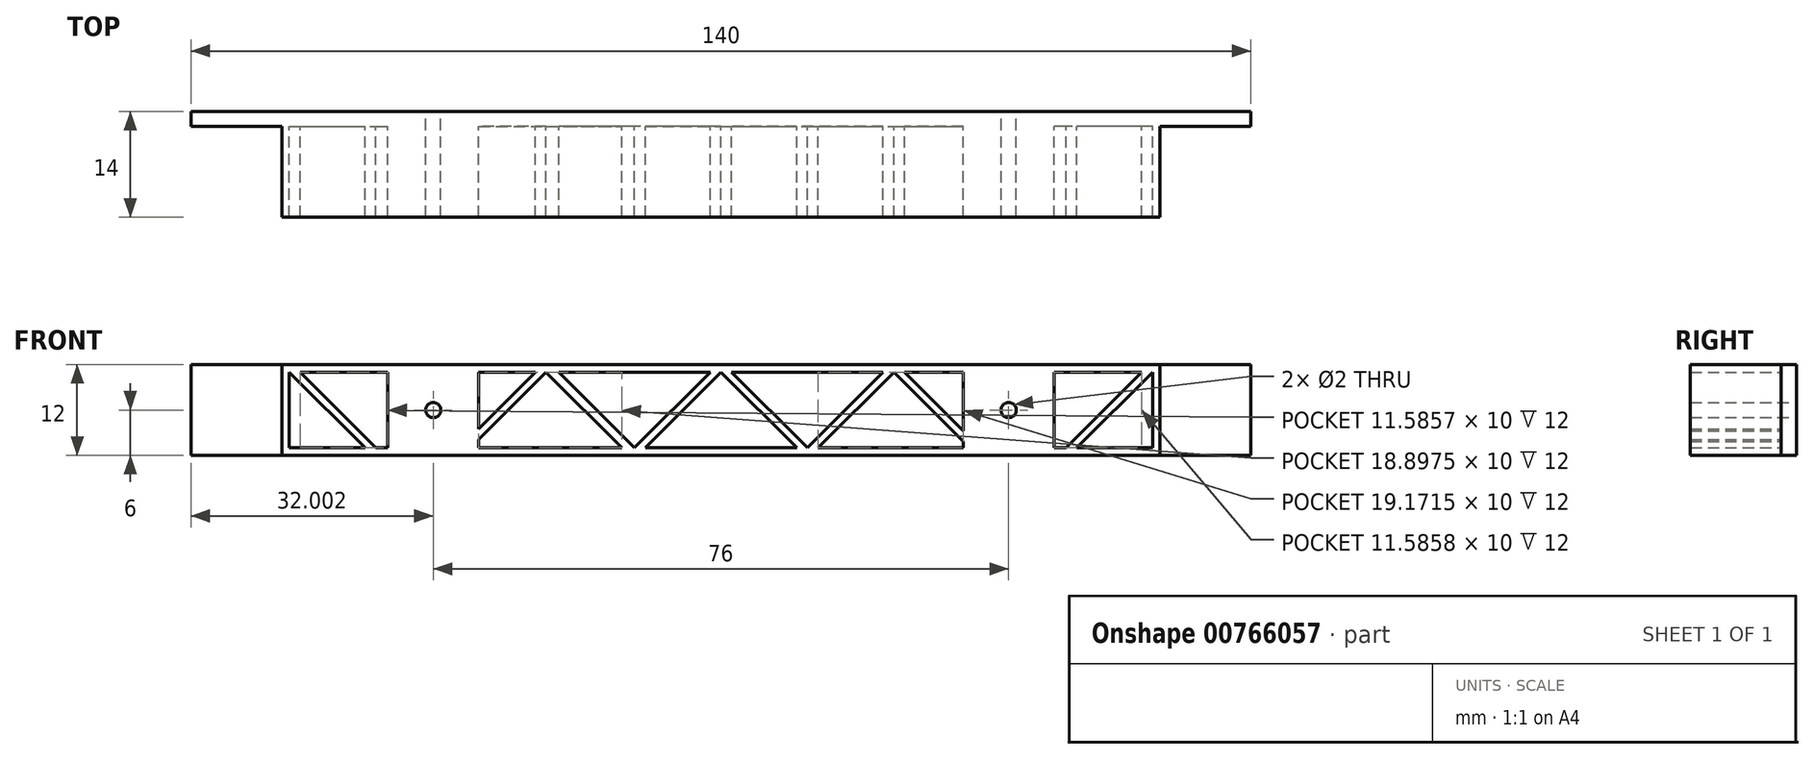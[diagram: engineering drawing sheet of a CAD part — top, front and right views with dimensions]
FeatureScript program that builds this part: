
annotation { "Feature Type Name" : "Feature", "Feature Type Description" : "" }
export const myFeature = defineFeature(function(context is Context, id is Id, definition is map)
    precondition{}
    {
        {
            var Q0;
            Q0=qCreatedBy(makeId("Front.planeOp"),FACE);
            var sketch = newSketch(context, id + "F0", { "sketchPlane" : qUnion([Q0])});
            skLineSegment(sketch, "E0.bottom", {"start": v(-41.02, 0) * mm, "end": v(98.98, 0) * mm});
            skLineSegment(sketch, "E0.top", {"start": v(-41.02, -12) * mm, "end": v(98.98, -12) * mm});
            skLineSegment(sketch, "E0.left", {"start": v(-41.02, 0) * mm, "end": v(-41.02, -12) * mm});
            skLineSegment(sketch, "E0.right", {"start": v(98.98, 0) * mm, "end": v(98.98, -12) * mm});
            skCircle(sketch, "E1", {"center": v(-9.02, -6) * mm, "radius": 1 * mm});
            skCircle(sketch, "E2", {"center": v(66.98, -6) * mm, "radius": 1 * mm});
            skSolve(sketch);
        }
        {
            var Q0;
            Q0=makeQuery(id+"F0.imprint","IMPRINT",FACE,{"disambiguationData":[TD([[makeQuery(id+"F0.imprint","IMPRINT",EDGE,{"derivedFrom":sQuery(id+"F0.wireOp",EDGE,"E0.bottom")}),-1.0]])]});
            extrude(context, id + "F1", {"entities" : qUnion([Q0]), "depth" : 2 * mm, "offsetDistance" : 25 * mm});
        }
        {
            var Q0;
            Q0=makeQuery(id+"F1.opExtrude","CAP_FACE",FACE,{"disambiguationData":[OSD([sQuery(id+"F0.wireOp",EDGE,"E0.bottom"),sQuery(id+"F0.wireOp",EDGE,"E0.top"),sQuery(id+"F0.wireOp",EDGE,"E0.left"),sQuery(id+"F0.wireOp",EDGE,"E0.right"),sQuery(id+"F0.wireOp",EDGE,"E1"),sQuery(id+"F0.wireOp",EDGE,"E2")])],"isStart":false});
            var sketch = newSketch(context, id + "F2", { "sketchPlane" : qUnion([Q0])});
            skLineSegment(sketch, "E3", {"start": v(-29.02, 0) * mm, "end": v(-29.02, -12) * mm});
            skLineSegment(sketch, "E4", {"start": v(86.98, 0) * mm, "end": v(86.98, -12) * mm});
            skLineSegment(sketch, "E5", {"start": v(-15.02, 0) * mm, "end": v(-15.02, -12) * mm});
            skLineSegment(sketch, "E6", {"start": v(-3.02, 0) * mm, "end": v(-3.02, -12) * mm});
            skLineSegment(sketch, "E7", {"start": v(-28.02, -1) * mm, "end": v(-28.02, -11) * mm});
            skLineSegment(sketch, "E8", {"start": v(-28.02, -11) * mm, "end": v(-15.02, -11) * mm});
            skLineSegment(sketch, "E9", {"start": v(-28.02, -1) * mm, "end": v(-15.02, -1) * mm});
            skLineSegment(sketch, "E10", {"start": v(60.98, 0) * mm, "end": v(60.98, -12) * mm});
            skLineSegment(sketch, "E11", {"start": v(72.98, 0) * mm, "end": v(72.98, -12) * mm});
            skLineSegment(sketch, "E12", {"start": v(85.98, -1) * mm, "end": v(85.98, -11) * mm});
            skLineSegment(sketch, "E13", {"start": v(85.98, -1) * mm, "end": v(72.98, -1) * mm});
            skLineSegment(sketch, "E14", {"start": v(85.98, -11) * mm, "end": v(72.98, -11) * mm});
            skLineSegment(sketch, "E15", {"start": v(60.98, -1) * mm, "end": v(-3.02, -1) * mm});
            skPoint(sketch, "E15.endSnap0", {"position": v(-3.02, -6) * mm});
            skLineSegment(sketch, "E16", {"start": v(-3.02, -11) * mm, "end": v(60.98, -11) * mm});
            skLineSegment(sketch, "E17", {"start": v(28.98, -1) * mm, "end": v(38.98, -11) * mm});
            skLineSegment(sketch, "E18", {"start": v(28.98, -1) * mm, "end": v(18.98, -11) * mm});
            skLineSegment(sketch, "E19", {"start": v(30.4, -1) * mm, "end": v(40.4, -11) * mm});
            skLineSegment(sketch, "E20", {"start": v(27.57, -1) * mm, "end": v(17.57, -11) * mm});
            skLineSegment(sketch, "E21", {"start": v(17.57, -11) * mm, "end": v(7.57, -1) * mm});
            skLineSegment(sketch, "E22", {"start": v(40.4, -11) * mm, "end": v(50.4, -1) * mm});
            skLineSegment(sketch, "E23", {"start": v(41.81, -11) * mm, "end": v(51.81, -1) * mm});
            skLineSegment(sketch, "E24", {"start": v(5.88, -1) * mm, "end": v(15.88, -11) * mm});
            skLineSegment(sketch, "E25", {"start": v(5.88, -1) * mm, "end": v(-3.02, -9.9) * mm});
            skLineSegment(sketch, "E26", {"start": v(51.81, -1) * mm, "end": v(60.98, -10.17) * mm});
            skLineSegment(sketch, "E27", {"start": v(60.98, -8.76) * mm, "end": v(53.22, -1) * mm});
            skLineSegment(sketch, "E28", {"start": v(-3.02, -8.48) * mm, "end": v(4.47, -1) * mm});
            skLineSegment(sketch, "E29", {"start": v(-28.02, -1) * mm, "end": v(-18.02, -11) * mm});
            skLineSegment(sketch, "E30", {"start": v(-26.6, -1) * mm, "end": v(-16.6, -11) * mm});
            skLineSegment(sketch, "E31", {"start": v(85.98, -1) * mm, "end": v(75.98, -11) * mm});
            skLineSegment(sketch, "E32", {"start": v(84.57, -1) * mm, "end": v(74.57, -11) * mm});
            skSolve(sketch);
        }
        {
            var Q0;
            Q0=makeQuery(id+"F2.imprint","IMPRINT",FACE,{"disambiguationData":[TD([[makeQuery(id+"F2.imprint","IMPRINT",EDGE,{"derivedFrom":makeQuery(id+"F1.opExtrude","CAP_EDGE",EDGE,{"disambiguationData":[OSD([sQuery(id+"F0.wireOp",EDGE,"E1")])],"isStart":false})}),-1.0]])]});
            var Q1;
            {var subQ11=sQuery(id+"F2.wireOp",EDGE,"E6");var subQ12=makeQuery(id+"F1.opExtrude","CAP_EDGE",EDGE,{"disambiguationData":[OSD([sQuery(id+"F0.wireOp",EDGE,"E0.bottom")])],"isStart":false});var subQ13=makeQuery(id+"F2.imprint","INTERSECT",VERTEX,{"derivedFrom":[subQ12,subQ11]});Q1=makeQuery(id+"F2.imprint","IMPRINT",FACE,{"disambiguationData":[TD([[makeQuery(id+"F2.imprint","IMPRINT",EDGE,{"disambiguationData":[TD([[subQ13,-1.0]])],"derivedFrom":subQ11}),1.0]])]});}
            var Q2;
            {var subQ3=sQuery(id+"F2.wireOp",EDGE,"E6");var subQ6=makeQuery(id+"F1.opExtrude","CAP_EDGE",EDGE,{"disambiguationData":[OSD([sQuery(id+"F0.wireOp",EDGE,"E0.top")])],"isStart":false});var subQ9=makeQuery(id+"F2.imprint","INTERSECT",VERTEX,{"derivedFrom":[subQ6,subQ3]});Q2=makeQuery(id+"F2.imprint","IMPRINT",FACE,{"disambiguationData":[TD([[makeQuery(id+"F2.imprint","IMPRINT",EDGE,{"disambiguationData":[TD([[subQ9,1.0]])],"derivedFrom":subQ3}),1.0]])]});}
            var Q3;
            {var subQ0=sQuery(id+"F2.wireOp",EDGE,"E21");Q3=makeQuery(id+"F2.imprint","IMPRINT",FACE,{"disambiguationData":[TD([[makeQuery(id+"F2.imprint","IMPRINT",EDGE,{"derivedFrom":subQ0}),1.0]])]});}
            var Q4;
            {var subQ0=sQuery(id+"F2.wireOp",EDGE,"E25");Q4=makeQuery(id+"F2.imprint","IMPRINT",FACE,{"disambiguationData":[TD([[makeQuery(id+"F2.imprint","IMPRINT",EDGE,{"derivedFrom":subQ0}),-1.0]])]});}
            var Q5;
            {var subQ0=sQuery(id+"F2.wireOp",EDGE,"E31");Q5=makeQuery(id+"F2.imprint","IMPRINT",FACE,{"disambiguationData":[TD([[makeQuery(id+"F2.imprint","IMPRINT",EDGE,{"derivedFrom":subQ0}),-1.0]])]});}
            var Q6;
            {var subQ0=sQuery(id+"F2.wireOp",EDGE,"E17");Q6=makeQuery(id+"F2.imprint","IMPRINT",FACE,{"disambiguationData":[TD([[makeQuery(id+"F2.imprint","IMPRINT",EDGE,{"derivedFrom":subQ0}),1.0]])]});}
            var Q7;
            {var subQ0=sQuery(id+"F2.wireOp",EDGE,"E26");Q7=makeQuery(id+"F2.imprint","IMPRINT",FACE,{"disambiguationData":[TD([[makeQuery(id+"F2.imprint","IMPRINT",EDGE,{"derivedFrom":subQ0}),1.0]])]});}
            var Q8;
            {var subQ0=sQuery(id+"F2.wireOp",EDGE,"E22");Q8=makeQuery(id+"F2.imprint","IMPRINT",FACE,{"disambiguationData":[TD([[makeQuery(id+"F2.imprint","IMPRINT",EDGE,{"derivedFrom":subQ0}),-1.0]])]});}
            var Q9;
            {var subQ8=sQuery(id+"F2.wireOp",EDGE,"E4");Q9=makeQuery(id+"F2.imprint","IMPRINT",FACE,{"disambiguationData":[TD([[makeQuery(id+"F2.imprint","IMPRINT",EDGE,{"derivedFrom":subQ8}),-1.0]])]});}
            var Q10;
            Q10=makeQuery(id+"F2.imprint","IMPRINT",FACE,{"disambiguationData":[TD([[makeQuery(id+"F2.imprint","IMPRINT",EDGE,{"derivedFrom":makeQuery(id+"F1.opExtrude","CAP_EDGE",EDGE,{"disambiguationData":[OSD([sQuery(id+"F0.wireOp",EDGE,"E2")])],"isStart":false})}),-1.0]])]});
            var Q11;
            {var subQ0=sQuery(id+"F2.wireOp",EDGE,"E29");Q11=makeQuery(id+"F2.imprint","IMPRINT",FACE,{"disambiguationData":[TD([[makeQuery(id+"F2.imprint","IMPRINT",EDGE,{"derivedFrom":subQ0}),1.0]])]});}
            var Q12;
            {var subQ0=sQuery(id+"F2.wireOp",EDGE,"E3");Q12=makeQuery(id+"F2.imprint","IMPRINT",FACE,{"disambiguationData":[TD([[makeQuery(id+"F2.imprint","IMPRINT",EDGE,{"derivedFrom":subQ0}),1.0]])]});}
            var Q13;
            {var subQ0=sQuery(id+"F2.wireOp",EDGE,"E18");Q13=makeQuery(id+"F2.imprint","IMPRINT",FACE,{"disambiguationData":[TD([[makeQuery(id+"F2.imprint","IMPRINT",EDGE,{"derivedFrom":subQ0}),-1.0]])]});}
            extrude(context, id + "F3", {"entities" : qUnion([Q0, Q1, Q2, Q3, Q4, Q5, Q6, Q7, Q8, Q9, Q10, Q11, Q12, Q13]), "operationType" : NewBodyOperationType.ADD, "depth" : 12 * mm, "offsetDistance" : 25 * mm});
        }
    });
